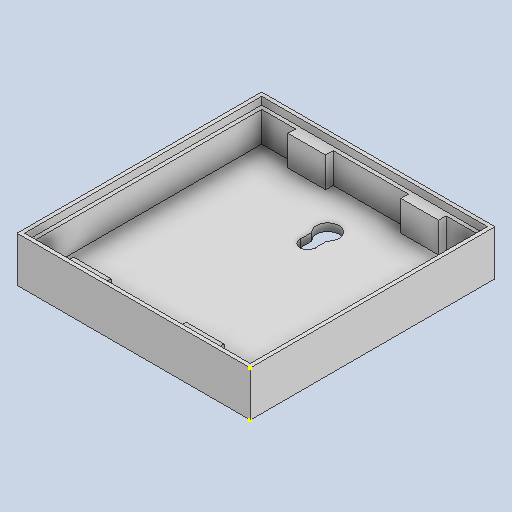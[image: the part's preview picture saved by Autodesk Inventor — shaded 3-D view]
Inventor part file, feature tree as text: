
AUTODESK INVENTOR PART (.ipt)
format: ipt  version: 2022 (Build 260153000, 153)  size: 206,848 bytes
history: native  units: in
note: dims shown in document units (in); Inventor stores cm internally (conversion verified against a paired STEP export)
features: sketch x7, extrude x5
ambient origin geometry x8: Origin, YZ Plane, XZ Plane, XY Plane, X Axis, Y Axis, Z Axis, Center Point
bodies: Solid1 (feature_tree)
feature tree (12):
  sketch  "Sketch1"  dims[d0=2.4409in d1=2.5591in]
  extrude  "Extrusion1"  Depth=2.5591in
  sketch  "Sketch3"  dims[d6=0.0787in d7=0.0787in]
  extrude  "Extrusion2"  Depth=0.0787in
  extrude  "Extrusion5"  Depth=0.0787in
  extrude  "Extrusion7"  Depth=0.0787in
  extrude  "Extrusion8"  Depth=0.0787in
  sketch  "Sketch2"  dims[d2=0.4724in d3=0.0in d5=0.0787in]
  sketch  "Sketch4"  dims[d8=0.0787in d9=0.0787in]
  sketch  "Sketch10"  dims[d10=0.0787in d11=0.0787in]
  sketch  "Sketch12"  dims[d12=0.0787in]
  sketch  "Sketch13"  dims[d13=0.3937in d14=0.0in d55=0.0787in d56=0.3937in d57=0.3937in d58=0.0787in d59=0.3543in d60=0.3937in d61=0.3937in d62=0.3543in d63=0.3543in d64=0.3543in d65=0.0in d79=0.3937in d80=0.0in d81=0.0394in d82=0.0394in d83=0.0394in d84=0.0394in d85=0.0394in d86=0.0394in d87=0.0394in d88=0.0787in d89=0.0in d40=0.0197in d41=0.0344in d42=0.0197in d43=0.0344in d66=0.0197in d67=0.0344in d74=0.0197in d75=0.0344in d76=0.0197in d77=0.0344in]
